# Revit family: NBS_Senator_OffcTbls_Ad-libTablesUK_Round-SingleLeg
name_source: partatom
category: Furniture
revit_build: Autodesk Revit 2016 (Build: 20151007_0715(x64)
units: mm (PartAtom-declared; Revit-internal decimal feet)

## family parameters
Always vertical = Yes
Cut with Voids When Loaded = No
Room Calculation Point = No
Shared = No
Work Plane-Based = No

## types (4) — shared parameters
AssetType = Moveable
CablePortCoverMaterial = NBS_Concept
Category = Pr_40_50_21_60:Office tables
CodePerformance = BS EN 15372 2008, BS 6396 2008
ColourOptions = Carini walnut, mocha, autumn, strata oak, maple, highland oak, beech, winter oak, hacienda white, white, light grey, denim, clay, bordeaux, lemon sorbet, Formica  fundamentals, polyrey, durion
ColumnMaterial = NBS_Concept
Description = Round table with 4 star base
DurationUnit = year
ExpectedLife = 15
ExposedEdgesOptions = Ply effect edging, silver ply edging
Finish = MFC
FinishOptions = MFC, MFMDF, laminate
FootHeight = 10 mm  [stored 0.0328084 ft]
FrameMountingMaterial = NBS_Concept
FramesColourOptions = Black, slate grey, light grey
FramesSupports = 4 Star base tables utilise an aluminium base and top casting with a steel column
HasProfileEdge = No
IfcExportAs = IfcFurnitureType
IfcExportType = TABLE
IsBuiltIn = No
ManufacturerName = Senator
ManufacturerURL = www.senator.co.uk
ModelReference = Ad-lib tables round UK
NBSCertification = www.nationalbimlibrary.com/cert/g2kfqilt
NBSDescription = Office tables
NBSReference = 45-35-20/340
PostHeight = 550 mm
PostMaterial = NBS_Concept
ProductInformation = www.Senator.com/FamilyDocuments/474/Senator_SPEC_2017_%20ADLIB%20Tables_v9%20WEB.pdf
Status = UNSET
SustainabilityPerformance = 99% recycleable
TechMeshOptions = Black, slate grey
Uniclass2015Code = Pr_40_50_21_60
Uniclass2015Title = Office tables
Uniclass2015Version = Products v1.9
Version = 2
WarrantyDescription = Senator warrants that its manufactured products are free from defects for a period of fifteen years on Senator desking ranges
WarrantyDurationParts = 15
WarrantyDurationUnit = year
WorktopLaminate = No
WorktopMFC = Yes
WorktopMFMDF = No
WorktopMaterial = NBS_Concept
WorktopMaterialTapedEdge = NBS_Concept
WorktopThickness = 25 mm  [stored 0.082021 ft]
WorktopType = NBS_Senator_OffcTbls_Ad-libTablesUK_RoundMFC : RoundMFC
WorktopTypeLaminate = NBS_Senator_OffcTbls_Ad-libTablesUK_RoundLaminate : RoundLaminate
WorktopTypeMFC = NBS_Senator_OffcTbls_Ad-libTablesUK_RoundMFC : RoundMFC
WorktopTypeMFMDF = NBS_Senator_OffcTbls_Ad-libTablesUK_RoundMFMDF : Round_MFMDF
zero-valued in all types: NumberOfChairs

## per-type parameters (varying)
| type | BIMObjectName | DimensionsPlanSize | Name | NominalDepth | NominalHeight | NominalLength | NominalWidth | Size | WorksurfaceArea | WorktopDiameter | WorktopHeight | WorktopRadius |
| ALP08RD | NBS_Senator_OfficeTables_Ad-libTablesUK_Round_ALP08RD | 800 x 800 mm | OfficeTables_Ad-libTablesUK_Round_ALP08RD_Senator | 800 mm  [stored 2.62467 ft] | 740 mm | 800 mm  [stored 2.62467 ft] | 800 mm  [stored 2.62467 ft] | 800 x 800 x 740 mm | 0.5 m² | 800 mm  [stored 2.62467 ft] | 740 mm | 400 mm  [stored 1.31234 ft] |
| ALP08RDC | NBS_Senator_OfficeTables_Ad-libTablesUK_Round_ALP08RDC | 800 x 800 mm | OfficeTables_Ad-libTablesUK_Round_ALP08RDC_Senator | 800 mm  [stored 2.62467 ft] | 400 mm  [stored 1.31234 ft] | 800 mm  [stored 2.62467 ft] | 800 mm  [stored 2.62467 ft] | 800 x 800 x 400 mm | 0.5 m² | 800 mm  [stored 2.62467 ft] | 400 mm  [stored 1.31234 ft] | 400 mm  [stored 1.31234 ft] |
| ALP08RDP | NBS_Senator_OfficeTables_Ad-libTablesUK_Round_ALP08RDP | 800 x 800 mm | OfficeTables_Ad-libTablesUK_Round_ALP08RDP_Senator | 800 mm  [stored 2.62467 ft] | 1050 mm | 800 mm  [stored 2.62467 ft] | 800 mm  [stored 2.62467 ft] | 800 x 800 x 1050 mm | 0.5 m² | 800 mm  [stored 2.62467 ft] | 1050 mm | 400 mm  [stored 1.31234 ft] |
| ALP10RD | NBS_Senator_OfficeTables_Ad-libTablesUK_Round_ALP10RD | 1000 x 1000 mm | OfficeTables_Ad-libTablesUK_Round_ALP10RD_Senator | 1000 mm  [stored 3.28084 ft] | 740 mm | 1000 mm  [stored 3.28084 ft] | 1000 mm  [stored 3.28084 ft] | 1000 x 1000 x 740 mm | 0.79 m² | 1000 mm  [stored 3.28084 ft] | 740 mm | 500 mm |

note: column(s) folded — value = type name in every type: ModelNumber

note: [stored X ft] marks values corroborated as IEEE doubles in the binary element streams (Revit-internal decimal feet)

## geometry (parser evidence)
native form markers: Sweep x13
no freeform markers — native parametric forms only
